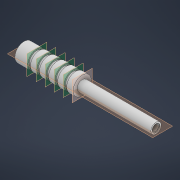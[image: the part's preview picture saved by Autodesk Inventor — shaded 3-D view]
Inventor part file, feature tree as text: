
AUTODESK INVENTOR PART (.ipt)
format: ipt  version: 2021 (Build 250183000, 183)  size: 164,864 bytes
history: native  units: in
note: dims shown in document units (in); Inventor stores cm internally (conversion verified against a paired STEP export)
features: extrude x9, sketch x9, plane x5
ambient origin geometry x8: Origin, YZ Plane, XZ Plane, XY Plane, X Axis, Y Axis, Z Axis, Center Point
bodies: Solid1 (feature_tree)
feature tree (23):
  extrude  "Extrusion1"  Depth=1.122in TaperAngle=0.0deg
  extrude  "Extrusion2"  Depth=0.0098in TaperAngle=0.0deg
  extrude  "Extrusion3"  Depth=0.2264in TaperAngle=0.0deg
  extrude  "Extrusion4"  Depth=0.8858in TaperAngle=0.0deg
  plane  "Work Plane1"
  extrude  "Extrusion5"  Depth=0.2362in
  plane  "Work Plane2"
  extrude  "Extrusion6"  Depth=0.0394in TaperAngle=0.0deg
  plane  "Work Plane3"
  extrude  "Extrusion7"  Depth=0.2756in
  plane  "Work Plane4"
  extrude  "Extrusion8"  Depth=0.0394in TaperAngle=0.0deg
  plane  "Work Plane5"
  extrude  "Extrusion9"  Depth=0.2756in
  sketch  "Sketch1"  dims[d0=0.1575in d1=1.122in d2=0.0in]
  sketch  "Sketch2"  dims[d3=0.1181in d4=0.0098in d5=0.0in]
  sketch  "Sketch3"  dims[d6=0.0984in d7=0.2264in d8=0.0in]
  sketch  "Sketch4"  dims[d9=0.2756in d10=0.8858in d11=0.0in]
  sketch  "Sketch5"  dims[d12=-0.1969in d13=0.2362in]
  sketch  "Sketch7"  dims[d14=0.2756in d15=0.0394in d16=0.0in]
  sketch  "Sketch9"  dims[d17=-0.0984in d18=0.2756in]
  sketch  "Sketch10"  dims[d19=0.2362in d20=0.0394in d21=0.0in]
  sketch  "Sketch11"  dims[d24=-0.0984in d25=0.2756in d26=0.2362in d27=0.0394in d28=0.0in d29=-0.0984in d30=0.2756in d31=0.2362in d32=0.0394in d33=0.0in d34=-0.0984in d35=0.2756in d36=0.2362in d37=0.0394in d38=0.0in]
